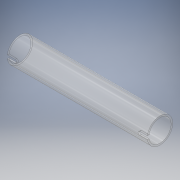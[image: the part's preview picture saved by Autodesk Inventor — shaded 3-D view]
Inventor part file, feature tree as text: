
AUTODESK INVENTOR PART (.ipt)
format: ipt  version: 2017 SP1 (Build 210196100, 196)  size: 167,424 bytes
history: native  units: mm
features: extrude x2, plane x2, sketch x2, fillet x1, mirror x1
ambient origin geometry x8: Origin, YZ Plane, XZ Plane, XY Plane, X Axis, Y Axis, Z Axis, Center Point
bodies: Solid1 (feature_tree)
feature tree (8):
  extrude  "Extrusion1"  Depth=26.0mm
  extrude  "Extrusion2"  Depth=4.0mm
  fillet  "Fillet1"  Radius=11.0mm
  plane  "Work Plane1"
  mirror  "Mirror1"
  plane  "Work Plane2"
  sketch  "Sketch1"  dims[d0=30.0mm d1=26.0mm]
  sketch  "Sketch2"  dims[d2=165.0mm d3=0.0mm d4=4.0mm d5=11.0mm d6=180.0mm d7=0.0mm d8=2.0mm]
